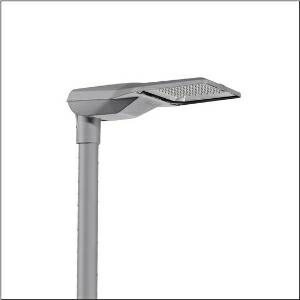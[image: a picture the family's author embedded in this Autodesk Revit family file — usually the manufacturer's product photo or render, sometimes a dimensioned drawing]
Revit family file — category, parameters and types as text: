
# Revit family: streetlight_sl_21_iq_midi___st0_5a_5xe3b31g08nb_5b56
name_source: partatom
category: Lighting Fixtures
units: mm (PartAtom-declared; Revit-internal decimal feet)

## family parameters
Cut with Voids When Loaded = No
Host = Face
Light Source = No
Part Type = Normal
Room Calculation Point = No
Round Connector Dimension = Use Diameter
Shared = No

## types (1)
- --- (1 x LED, 23230 lm, 155.5 W, 3000K)
    Apparent Load = 155 VA
    CIE Flux Codes = 43 76 97 100 100
    Color Rendering = 70
    Color Temperature = 3000K
    Default Elevation = 1800 mm
    Description = Streetlight SL 21 iQ midi, mast luminaire, primary light control with lens, of PMMA, primary optical cover: cover, of toughened safety glass, transparent, light distribution: ST0.5a, light emission: direct distribution, primary light characteristic: asymmetric, installation type: post-top, side-entry, LED, High Power LED, rated luminous flux: 23.230lm, luminous efficacy: 149lm/W, light colour: 730, colour temperature: 3000K, control gear: iQ Street-Remote, control: Street-Remote, Auto-Match, Temp-Guard, Lumen-Switch, Night-Set, Smart-Wire, Light-Fading, Desk-Remote (wireless, voltage-free reading and setting of iQ features in the workshop via application-optimized NFC function/RFID function), optimised constant luminous flux control (CLO 2.0), pre-setting: linear dimming characteristic, mains connection: 230..240V, AC, 50/60Hz, start of lifetime: 156W, end of service life: 162W, reduction: 69W, luminaire housing, of diecast aluminium, powder-coated, SITECO metallic grey (DB 702S), corrosivity category C5 high according to DIN EN ISO 12944, please order mast flange separately, inclination adjustable: 0°, 5°, 10°, 15°, sealing non-destructively replaceable, multi-level sealing system, length: 644mm, width: 335mm, height: 110mm, mast flange for spigot size: 42mm (side-entry): 5XC10008XM4, 60/48mm (side-entry/post-top): 5XC10108XM2, 76/60mm (side-entry/post-top): 5XC10108XM1, mounting height: 4..8m, protection rating (complete): IP66, insulation class (complete): insulation class II (safety insulation), certification: CE, ENEC, ENEC+, VDE, impact resistance: IK10, permissible operating ambient temperature for outdoor applications: -40..+50°C, standard-compliant lighting for roads and squares, packaging unit: 1 piece

Light Distribution: ST0.5a
    Height = 111 mm
    Lamp = 1 x LED
    Lamp Light Flux = 23230 lm
    Lamp Power = 155.5 W
    Lamp count = 1
    Length = 644 mm
    Luminous efficacy = 149 lm/W
    Manufacturer = Siteco
    ModVariant = No
    Model = 5XE3B31G08NB
    Number of Poles = 1
    OnlyDefault = Yes
    Power Factor = 1
    Product Name = Streetlight SL 21 iQ midi | ST0.5a
    Product group = mast luminaire | pylon top
    ProductGroupID = 6100
    Protection Class = Protection class II
    Protection Degree = IP 66
    RLX_Detail_Level = 1
    RLX_Emergency_Light_Flux = 0 lm
    RLX_Emergency_Type = 0
    RLX_Emergency_Type_DB = No
    RlxData = <blob elided: 38401 chars, md5=165bd38b>
    Socket = socket
    Standby Power = 0 W
    System Light Flux = 23230 lm
    System Power = 155 W
    Type Comments = factory setting: luminous flux: 100 % | dim-lin: 254 | 823 mA
    Type Image = l_1004298.jpg
    URL = http://relux.com
    VarID = @adj_171023
    Voltage = 0 V
    Weight = 0.00 kg
    Width = 336 mm

## geometry (parser evidence)
native form markers: Blend x4, Sweep x9
no freeform markers — native parametric forms only
